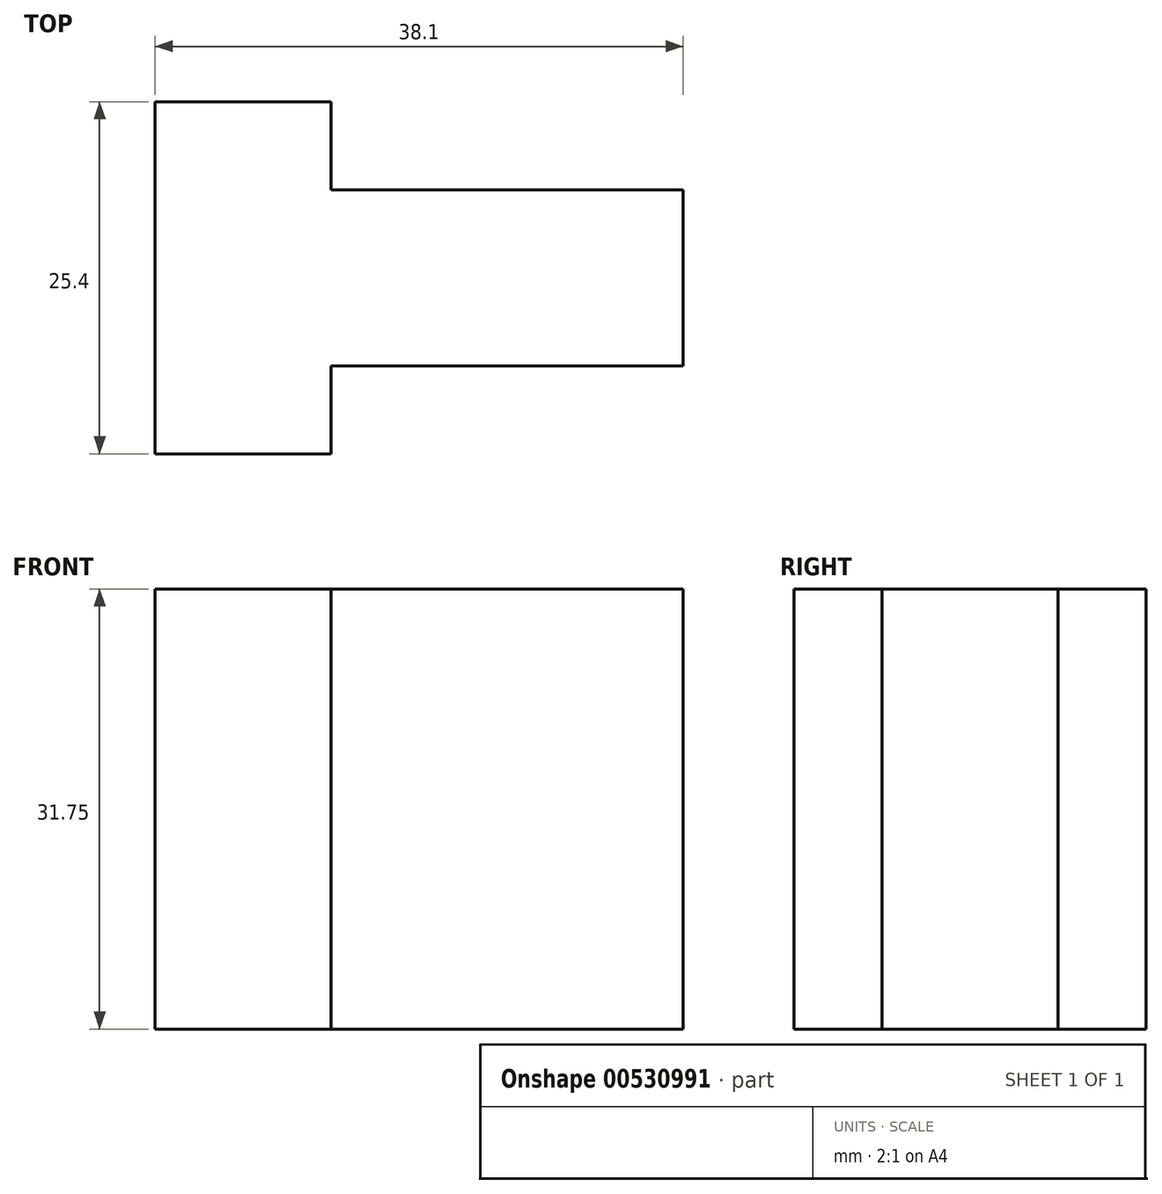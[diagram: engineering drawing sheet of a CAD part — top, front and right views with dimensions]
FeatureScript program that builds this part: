
annotation { "Feature Type Name" : "Feature", "Feature Type Description" : "" }
export const myFeature = defineFeature(function(context is Context, id is Id, definition is map)
    precondition{}
    {
        {
            var Q0;
            Q0=qCreatedBy(makeId("Top.planeOp"),FACE);
            var sketch = newSketch(context, id + "F0", { "sketchPlane" : qUnion([Q0])});
            skLineSegment(sketch, "E0", {"start": v(0, 0) * mm, "end": v(12.7, 0) * mm});
            skLineSegment(sketch, "E1", {"start": v(12.7, 0) * mm, "end": v(12.7, 6.35) * mm});
            skLineSegment(sketch, "E2", {"start": v(12.7, 6.35) * mm, "end": v(38.1, 6.35) * mm});
            skLineSegment(sketch, "E3", {"start": v(38.1, 6.35) * mm, "end": v(38.1, 19.05) * mm});
            skLineSegment(sketch, "E4", {"start": v(38.1, 19.05) * mm, "end": v(12.7, 19.05) * mm});
            skLineSegment(sketch, "E5", {"start": v(12.7, 19.05) * mm, "end": v(12.7, 25.4) * mm});
            skLineSegment(sketch, "E6", {"start": v(12.7, 25.4) * mm, "end": v(0, 25.4) * mm});
            skLineSegment(sketch, "E7", {"start": v(0, 25.4) * mm, "end": v(0, 0) * mm});
            skSolve(sketch);
        }
        {
            var Q0;
            Q0=makeQuery(id+"F0.imprint","IMPRINT",FACE,{"disambiguationData":[TD([[makeQuery(id+"F0.imprint","IMPRINT",EDGE,{"derivedFrom":sQuery(id+"F0.wireOp",EDGE,"E0")}),1.0]])]});
            extrude(context, id + "F1", {"entities" : qUnion([Q0]), "oppositeDirection" : true, "depth" : 31.75 * mm, "offsetDistance" : 25.4 * mm});
        }
    });
